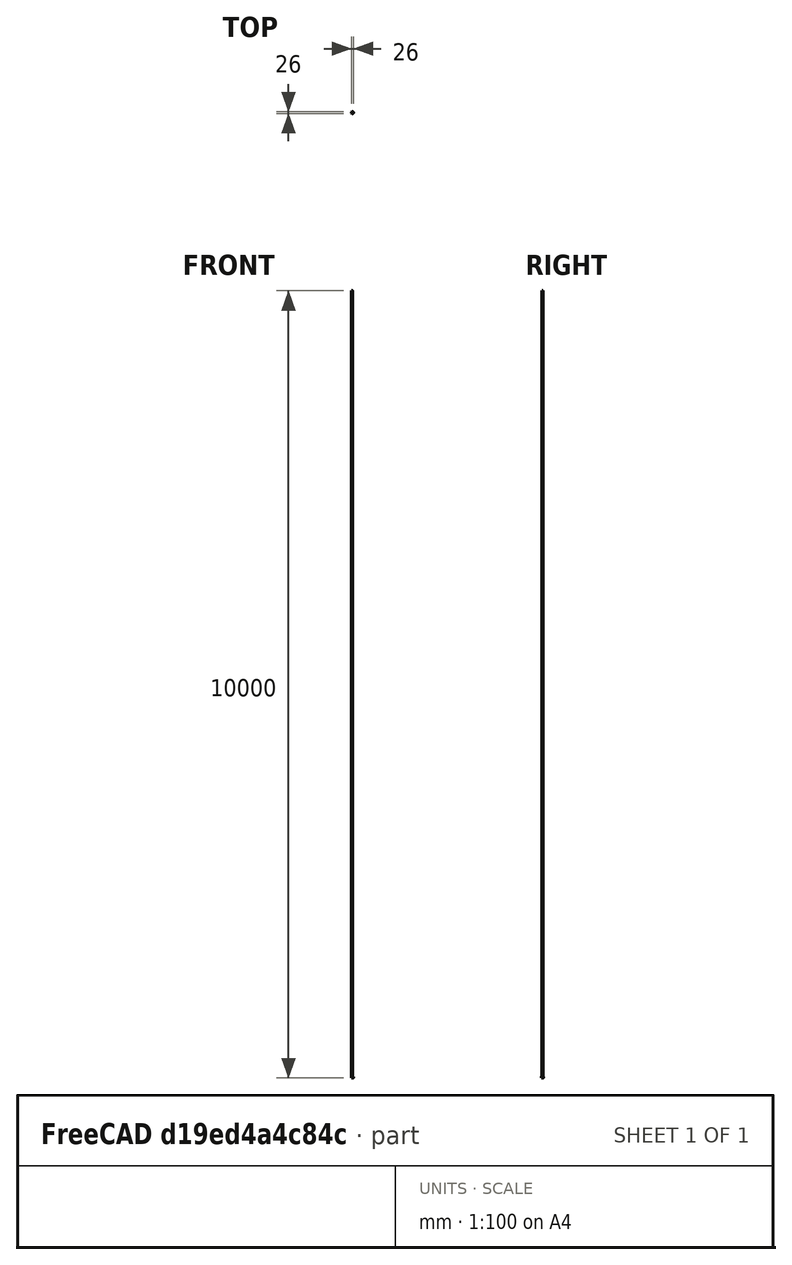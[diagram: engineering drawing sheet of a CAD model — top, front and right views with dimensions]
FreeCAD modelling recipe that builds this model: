
FCSTD DOCUMENT  (FreeCAD 0.16R)
Label: LeverEcc
License: All rights reserved
LicenseURL: http://en.wikipedia.org/wiki/All_rights_reserved
objects: Sketcher::SketchObject×5, PartDesign::Pad×2, PartDesign::Pocket×2, PartDesign::Chamfer×2, Mesh::Feature×1
note: 15 computed .brp shape members not serialized (recipe doc carries the construction recipe); baked Part::Feature solids carry a one-line shape summary decoded from their .brp

FEATURE [Sketcher::SketchObject] Sketch
  sketch-geometry (1):
    g0: Circle CenterX=0 CenterY=0 CenterZ=0 NormalX=0 NormalY=0 NormalZ=1 Radius=11.9
  constraints (2):
    c: Coincident(g0,g-1)
    c: Radius(g0) = 11.9
FEATURE [PartDesign::Pad] Pad
  Length = 15
  Length2 = 100
  Sketch = -> Sketch
  Type = 0
FEATURE [Sketcher::SketchObject] Sketch001
FEATURE [Sketcher::SketchObject] Sketch002
  Placement = pos=(0,0,15) rot=(0,0,1;0rad)
  Support = -> Pad [Face3]
  sketch-geometry (1):
    g0: Circle CenterX=0 CenterY=0 CenterZ=0 NormalX=0 NormalY=0 NormalZ=1 Radius=13
  constraints (2):
    c: Radius(g0) = 13
    c: Coincident(g0,g-1)
FEATURE [PartDesign::Pad] Pad001
  Length = 1
  Length2 = 100
  Sketch = -> Sketch002
  Type = 0
FEATURE [Sketcher::SketchObject] Sketch003
  Placement = pos=(0,0,0) rot=(1,0,0;3.14159rad)
  Support = -> Pad001 [Face1]
  sketch-geometry (1):
    g0: Circle CenterX=-3 CenterY=0 CenterZ=0 NormalX=0 NormalY=0 NormalZ=1 Radius=6.36
  constraints (3):
    c: Radius(g0) = 6.36
    c: PointOnObject(g0,g-1)
    c: DistanceX(g0) = -3
FEATURE [PartDesign::Pocket] Pocket
  Length = 5
  Sketch = -> Sketch003
  Type = 1
FEATURE [Sketcher::SketchObject] Sketch004
  Placement = pos=(0,0,0) rot=(1,0,0;3.14159rad)
  Support = -> Pocket [Face1]
  sketch-geometry (4):
    g0: LineSegment StartX=-30 StartY=1 StartZ=0 EndX=0 EndY=1 EndZ=0
    g1: LineSegment StartX=0 StartY=1 StartZ=0 EndX=0 EndY=-1 EndZ=0
    g2: LineSegment StartX=0 StartY=-1 StartZ=0 EndX=-30 EndY=-1 EndZ=0
    g3: LineSegment StartX=-30 StartY=-1 StartZ=0 EndX=-30 EndY=1 EndZ=0
  constraints (12):
    c: Coincident(g0,g1)
    c: Coincident(g1,g2)
    c: Coincident(g2,g3)
    c: Coincident(g3,g0)
    c: Horizontal(g0)
    c: Horizontal(g2)
    c: Vertical(g1)
    c: Vertical(g3)
    c: Distance(g1) = 2
    c: Symmetric(g2,g0,g-1)
    c: PointOnObject(g1,g-2)
    c: Distance(g0) = 30
FEATURE [PartDesign::Pocket] Pocket001
  Length = 5
  Sketch = -> Sketch004
  Type = 1
FEATURE [PartDesign::Chamfer] Chamfer
  Base = -> Pocket001 [Edge9,Edge18,Edge10,Edge17]
  Size = 0.5
FEATURE [PartDesign::Chamfer] Chamfer001
  Base = -> Chamfer [Edge22,Edge30]
  Size = 0.5
FEATURE [Mesh::Feature] Mesh  label="Chamfer001 (Meshed)"
